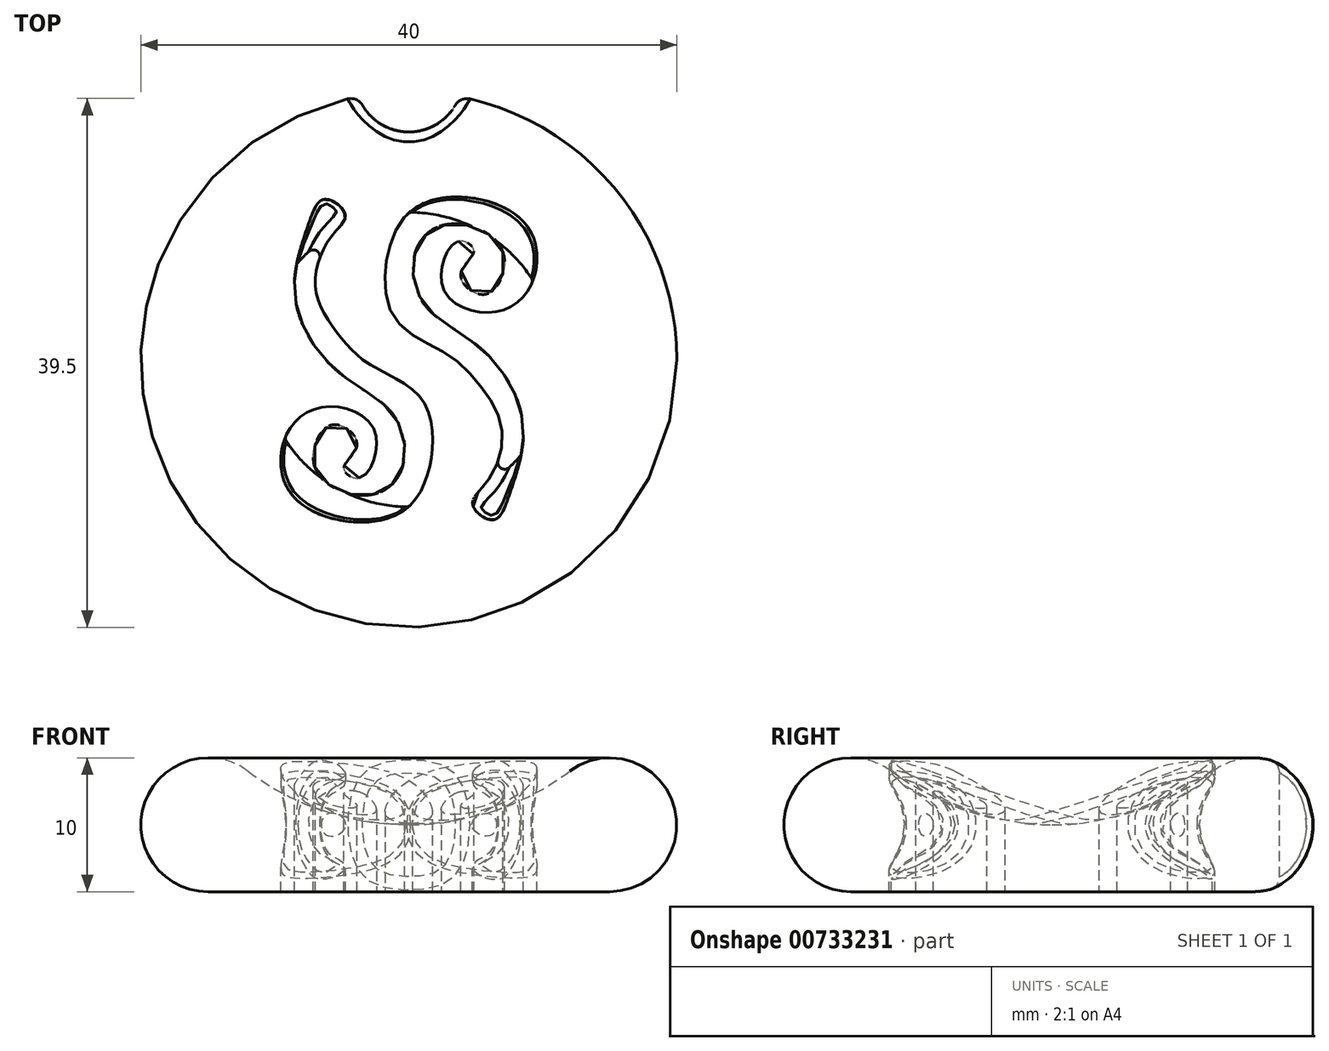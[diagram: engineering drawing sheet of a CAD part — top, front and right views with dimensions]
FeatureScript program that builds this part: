
annotation { "Feature Type Name" : "Feature", "Feature Type Description" : "" }
export const myFeature = defineFeature(function(context is Context, id is Id, definition is map)
    precondition{}
    {
        {
            var Q0;
            Q0=qCreatedBy(makeId("Front.planeOp"),FACE);
            var sketch = newSketch(context, id + "F0", { "sketchPlane" : qUnion([Q0])});
            skArc(sketch, "E0", {"start": v(-12, -3.5) * mm, "mid": v(-6.32, -6.47) * mm, "end": v(0, -7.5) * mm});
            skArc(sketch, "E1", {"start": v(-12, -3.5) * mm, "mid": v(-19.74, -5.92) * mm, "end": v(-15, -12.5) * mm});
            skLineSegment(sketch, "E2", {"start": v(0, -35.65) * mm, "end": v(0, 51.28) * mm, "construction": true});
            skLineSegment(sketch, "E3", {"start": v(0, -7.5) * mm, "end": v(0, -10) * mm});
            skLineSegment(sketch, "E4", {"start": v(-15, -12.5) * mm, "end": v(0, -12.5) * mm});
            skLineSegment(sketch, "E5", {"start": v(0, -7.5) * mm, "end": v(0, -12.5) * mm});
            skSolve(sketch);
        }
        {
            var Q0;
            Q0=makeQuery(id+"F0.imprint","IMPRINT",FACE,{"disambiguationData":[TD([[makeQuery(id+"F0.imprint","IMPRINT",EDGE,{"derivedFrom":sQuery(id+"F0.wireOp",EDGE,"E0")}),-1.0]])]});
            var Q1;
            Q1=sQuery(id+"F0.wireOp",EDGE,"E3");
            revolve(context, id + "F1", {"surfaceOperationType" : NewSurfaceOperationType.NEW, "entities" : qUnion([Q0]), "axis" : qUnion([Q1]), "revolveType" : RevolveType.FULL});
        }
        {
            var Q0;
            Q0=qCreatedBy(makeId("Top.planeOp"),FACE);
            var sketch = newSketch(context, id + "F2", { "sketchPlane" : qUnion([Q0])});
            skFitSpline(sketch, "E6", {"points": [v(3.7, 8.84) * mm, v(2.46, 6.81) * mm, v(3.08, 4.52) * mm, v(6.43, 3.55) * mm, v(9.17, 5.67) * mm, v(9, 9.73) * mm, v(5.02, 12.02) * mm, v(0.7, 11.5) * mm, v(-1.42, 8.5) * mm, v(-1.07, 3.1) * mm, v(2.9, 0.37) * mm, v(5.29, -1.92) * mm, v(6.96, -5.27) * mm, v(5.82, -9.16) * mm, v(4.76, -10.83) * mm, v(6.26, -11.98) * mm, v(7.5, -10.13) * mm, v(8.55, -5.27) * mm, v(6.87, -0.77) * mm, v(3.87, 1.96) * mm, v(1.05, 4.26) * mm, v(0.43, 7.87) * mm, v(2.37, 10) * mm, v(5.64, 9.55) * mm, v(7.14, 7.43) * mm, v(6, 4.96) * mm, v(4.32, 5.4) * mm, v(3.96, 6.73) * mm, v(4.85, 8.14) * mm, v(3.7, 8.84) * mm]});
            skFitSpline(sketch, "E7", {"points": [v(-3.7, -8.84) * mm, v(-2.46, -6.81) * mm, v(-3.08, -4.52) * mm, v(-6.43, -3.55) * mm, v(-9.17, -5.67) * mm, v(-9, -9.73) * mm, v(-5.02, -12.02) * mm, v(-0.7, -11.5) * mm, v(1.42, -8.5) * mm, v(1.07, -3.1) * mm, v(-2.9, -0.37) * mm, v(-5.29, 1.92) * mm, v(-6.96, 5.27) * mm, v(-5.82, 9.16) * mm, v(-4.76, 10.83) * mm, v(-6.26, 11.98) * mm, v(-7.5, 10.13) * mm, v(-8.55, 5.27) * mm, v(-6.87, 0.77) * mm, v(-3.87, -1.96) * mm, v(-1.05, -4.26) * mm, v(-0.43, -7.87) * mm, v(-2.37, -10) * mm, v(-5.64, -9.55) * mm, v(-7.14, -7.43) * mm, v(-6, -4.96) * mm, v(-4.32, -5.4) * mm, v(-3.96, -6.73) * mm, v(-4.85, -8.14) * mm, v(-3.7, -8.84) * mm]});
            skSolve(sketch);
        }
        {
            var Q0;
            Q0=makeQuery(id+"F2.imprint","IMPRINT",FACE,{"disambiguationData":[TD([[makeQuery(id+"F2.imprint","IMPRINT",EDGE,{"derivedFrom":sQuery(id+"F2.wireOp",EDGE,"E6")}),1.0]])]});
            var Q1;
            Q1=makeQuery(id+"F2.imprint","IMPRINT",FACE,{"disambiguationData":[TD([[makeQuery(id+"F2.imprint","IMPRINT",EDGE,{"derivedFrom":sQuery(id+"F2.wireOp",EDGE,"E7")}),1.0]])]});
            extrude(context, id + "F3", {"entities" : qUnion([Q0, Q1]), "operationType" : NewBodyOperationType.REMOVE, "oppositeDirection" : true, "depth" : 36.2 * mm, "offsetDistance" : 25 * mm, "symmetric" : true});
        }
        {
            var Q0;
            Q0=qCreatedBy(makeId("Front.planeOp"),FACE);
            var sketch = newSketch(context, id + "F4", { "sketchPlane" : qUnion([Q0])});
            skCircle(sketch, "E8", {"center": v(-15, -7.5) * mm, "radius": 4 * mm});
            skSolve(sketch);
        }
        {
            var Q0;
            Q0 = qSketchRegion(id + "F4", true);
            var Q1;
            Q1=sQuery(id+"F4.wireOp",EDGE,"E8");
            var Q2;
            Q2=sQuery(id+"F0.wireOp",EDGE,"E2");
            revolve(context, id + "F5", {"operationType" : NewBodyOperationType.ADD, "surfaceOperationType" : NewSurfaceOperationType.ADD, "entities" : qUnion([Q0]), "surfaceEntities" : qUnion([Q1]), "axis" : qUnion([Q2]), "revolveType" : RevolveType.FULL});
        }
        {
            var Q0;
            Q0=qCreatedBy(makeId("Top.planeOp"),FACE);
            var sketch = newSketch(context, id + "F6", { "sketchPlane" : qUnion([Q0])});
            skCircle(sketch, "E9", {"center": v(0, 21) * mm, "radius": 4 * mm});
            skSolve(sketch);
        }
        {
            var Q0;
            Q0=makeQuery(id+"F6.imprint","IMPRINT",FACE,{"disambiguationData":[TD([[makeQuery(id+"F6.imprint","IMPRINT",EDGE,{"derivedFrom":sQuery(id+"F6.wireOp",EDGE,"E9")}),1.0]])]});
            extrude(context, id + "F7", {"entities" : qUnion([Q0]), "operationType" : NewBodyOperationType.REMOVE, "oppositeDirection" : true, "depth" : 25 * mm, "offsetDistance" : 25 * mm});
        }
        {
            var Q0;
            Q0=makeQuery(id+"F7.boolean.opBoolean","INTERSECT",EDGE,{"derivedFrom":[makeQuery(id+"F1.opRevolve","SWEPT_FACE",FACE,{"disambiguationData":[OSD([sQuery(id+"F0.wireOp",EDGE,"E1")])]}),makeQuery(id+"F7.opExtrude","SWEPT_FACE",FACE,{"disambiguationData":[OSD([sQuery(id+"F6.wireOp",EDGE,"E9")])]})]});
            fillet(context, id + "F8", {"entities" : qUnion([Q0]), "radius" : 1 * mm, "tangentPropagation" : true, "allowEdgeOverflow" : false});
        }
        {
            var Q0;
            Q0=makeQuery(id+"F5.boolean.opBoolean","INTERSECT",EDGE,{"disambiguationData":[OD(2.0)],"derivedFrom":[makeQuery(id+"F3.boolean.opBoolean","COPY",FACE,{"derivedFrom":makeQuery(id+"F3.opExtrude","SWEPT_FACE",FACE,{"disambiguationData":[OSD([sQuery(id+"F2.wireOp",EDGE,"E6")])]})}),makeQuery(id+"F5.opRevolve","SWEPT_FACE",FACE,{"disambiguationData":[OSD([sQuery(id+"F4.wireOp",EDGE,"E8")])]})]});
            var Q1;
            Q1=makeQuery(id+"F5.boolean.opBoolean","SPLIT",FACE,{"disambiguationData":[TD([makeQuery(id+"F3.boolean.opBoolean","COPY",FACE,{"derivedFrom":makeQuery(id+"F3.opExtrude","SWEPT_FACE",FACE,{"disambiguationData":[OSD([sQuery(id+"F2.wireOp",EDGE,"E7")])]})})]),OD(0.0)],"derivedFrom":makeQuery(id+"F5.opRevolve","SWEPT_FACE",FACE,{"disambiguationData":[OSD([sQuery(id+"F4.wireOp",EDGE,"E8")])]})});
            var Q2;
            Q2=makeQuery(id+"F5.boolean.opBoolean","INTERSECT",EDGE,{"disambiguationData":[OD(2.0)],"derivedFrom":[makeQuery(id+"F3.boolean.opBoolean","COPY",FACE,{"derivedFrom":makeQuery(id+"F3.opExtrude","SWEPT_FACE",FACE,{"disambiguationData":[OSD([sQuery(id+"F2.wireOp",EDGE,"E7")])]})}),makeQuery(id+"F5.opRevolve","SWEPT_FACE",FACE,{"disambiguationData":[OSD([sQuery(id+"F4.wireOp",EDGE,"E8")])]})]});
            var Q3;
            Q3=makeQuery(id+"F5.boolean.opBoolean","INTERSECT",EDGE,{"disambiguationData":[OD(0.0)],"derivedFrom":[makeQuery(id+"F3.boolean.opBoolean","COPY",FACE,{"derivedFrom":makeQuery(id+"F3.opExtrude","SWEPT_FACE",FACE,{"disambiguationData":[OSD([sQuery(id+"F2.wireOp",EDGE,"E6")])]})}),makeQuery(id+"F5.opRevolve","SWEPT_FACE",FACE,{"disambiguationData":[OSD([sQuery(id+"F4.wireOp",EDGE,"E8")])]})]});
            fillet(context, id + "F9", {"entities" : qUnion([Q0, Q1, Q2, Q3]), "radius" : .5 * mm, "tangentPropagation" : true, "allowEdgeOverflow" : false});
        }
    });
